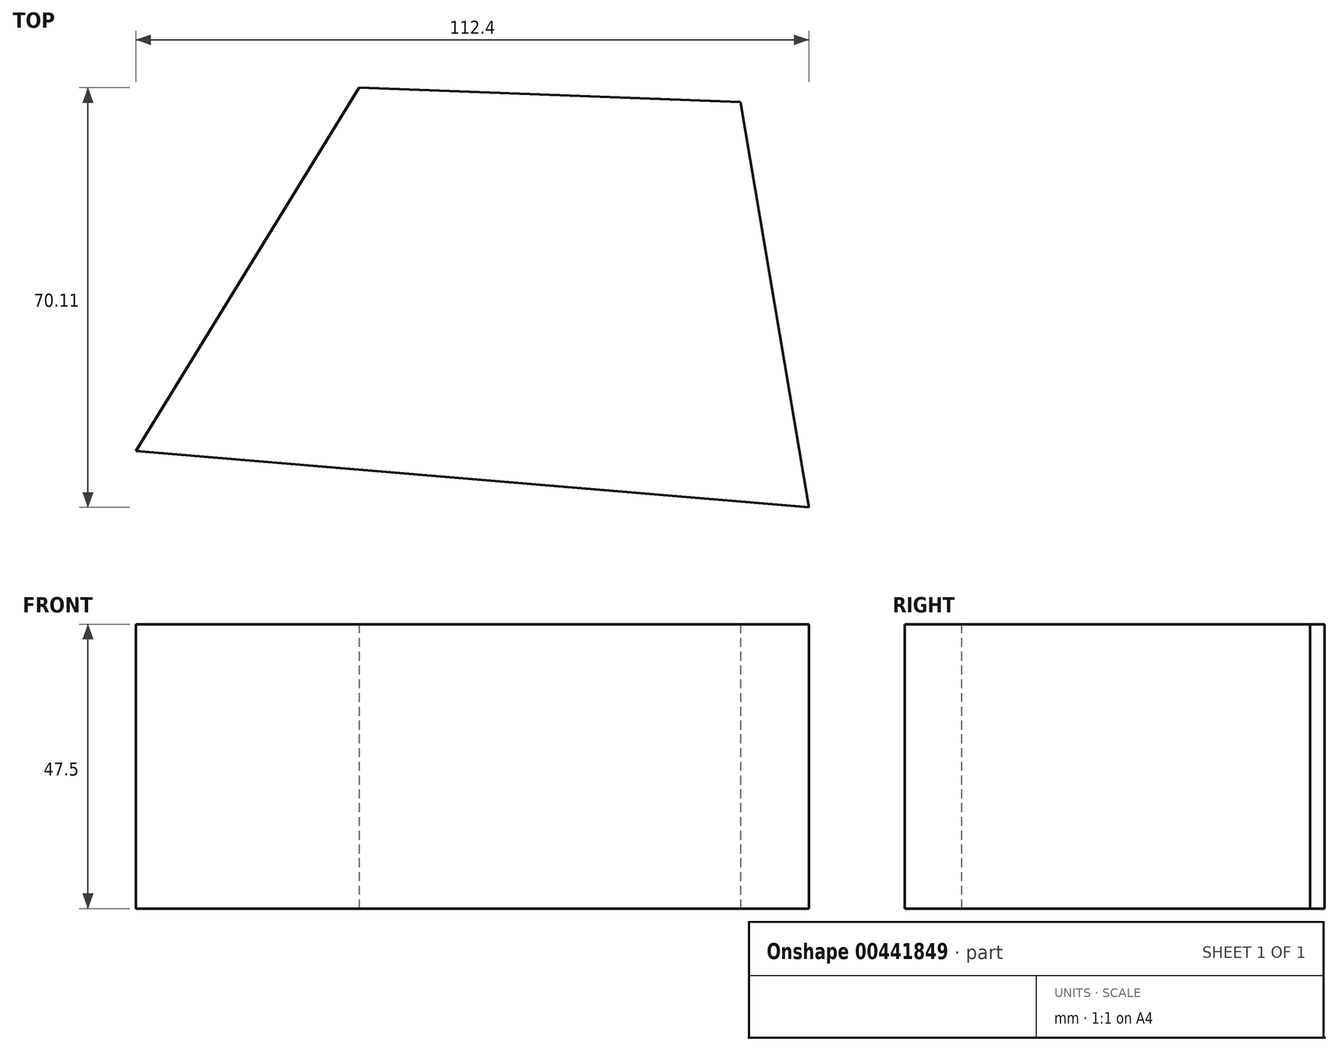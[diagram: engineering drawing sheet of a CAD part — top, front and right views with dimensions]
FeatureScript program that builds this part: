
annotation { "Feature Type Name" : "Feature", "Feature Type Description" : "" }
export const myFeature = defineFeature(function(context is Context, id is Id, definition is map)
    precondition{}
    {
        {
            var Q0;
            Q0=qCreatedBy(makeId("Top.planeOp"),FACE);
            var sketch = newSketch(context, id + "F0", { "sketchPlane" : qUnion([Q0])});
            skLineSegment(sketch, "E0", {"start": v(-53.84, -28.07) * mm, "end": v(-16.57, 32.61) * mm});
            skLineSegment(sketch, "E1", {"start": v(-16.57, 32.61) * mm, "end": v(47.09, 30.2) * mm});
            skLineSegment(sketch, "E2", {"start": v(47.09, 30.2) * mm, "end": v(58.56, -37.5) * mm});
            skLineSegment(sketch, "E3", {"start": v(58.56, -37.5) * mm, "end": v(-53.84, -28.07) * mm});
            skSolve(sketch);
        }
        {
            var Q0;
            Q0=makeQuery(id+"F0.imprint","IMPRINT",FACE,{"disambiguationData":[TD([[makeQuery(id+"F0.imprint","IMPRINT",EDGE,{"derivedFrom":sQuery(id+"F0.wireOp",EDGE,"E0")}),-1.0]])]});
            extrude(context, id + "F1", {"entities" : qUnion([Q0]), "depth" : 47.5 * mm});
        }
    });
